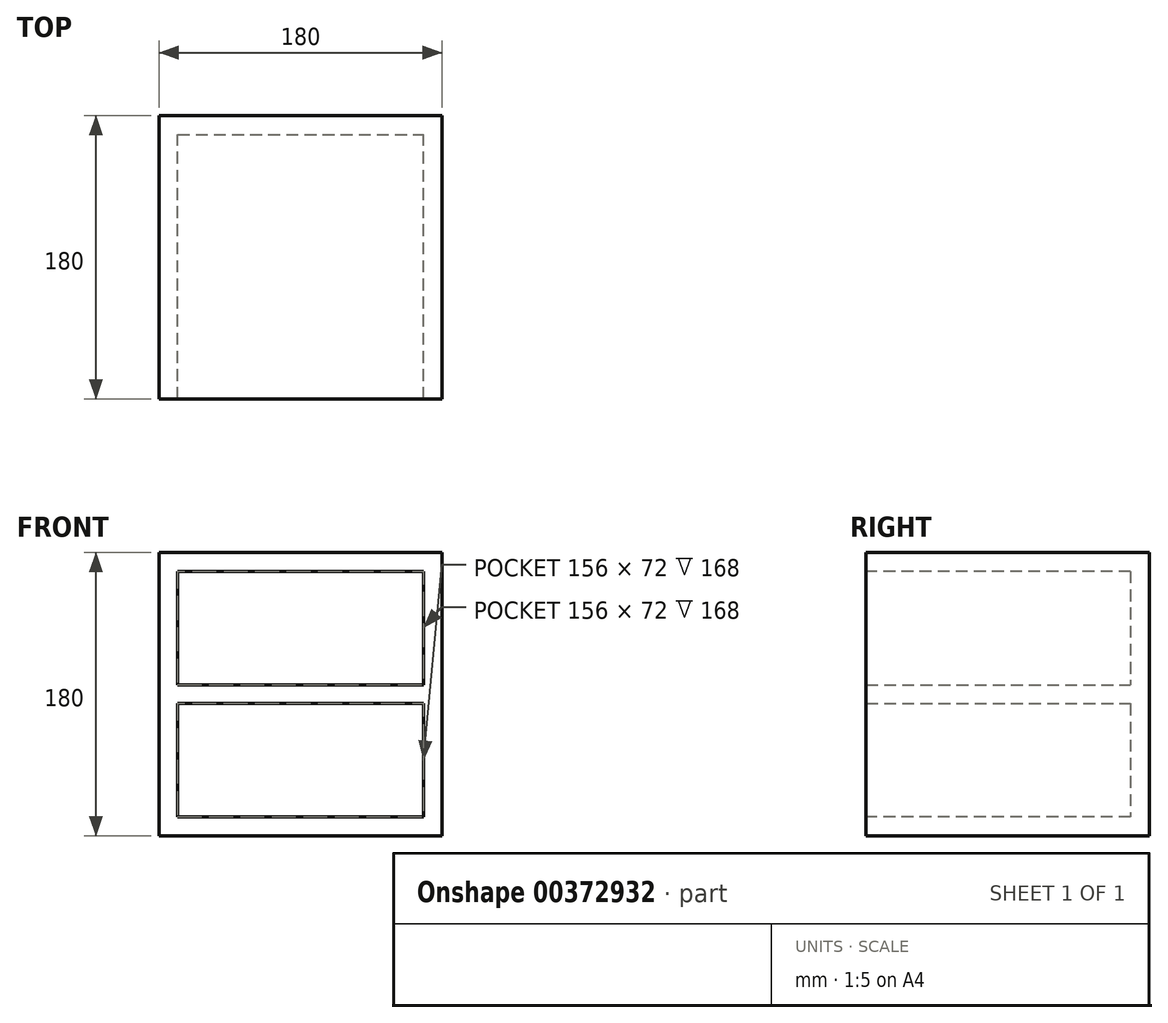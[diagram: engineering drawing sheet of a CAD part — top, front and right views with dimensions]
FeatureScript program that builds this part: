
annotation { "Feature Type Name" : "Feature", "Feature Type Description" : "" }
export const myFeature = defineFeature(function(context is Context, id is Id, definition is map)
    precondition{}
    {
        {
            var Q0;
            Q0=qCreatedBy(makeId("Top.planeOp"),FACE);
            var sketch = newSketch(context, id + "F0", { "sketchPlane" : qUnion([Q0])});
            skLineSegment(sketch, "E0.bottom", {"start": v(-90, 90) * mm, "end": v(90, 90) * mm});
            skLineSegment(sketch, "E0.top", {"start": v(-90, -90) * mm, "end": v(90, -90) * mm});
            skLineSegment(sketch, "E0.left", {"start": v(-90, 90) * mm, "end": v(-90, -90) * mm});
            skLineSegment(sketch, "E0.right", {"start": v(90, 90) * mm, "end": v(90, -90) * mm});
            skPoint(sketch, "E0.middle", {"position": v(0, 0) * mm});
            skSolve(sketch);
        }
        {
            var Q0;
            Q0=makeQuery(id+"F0.imprint","IMPRINT",FACE,{"disambiguationData":[TD([[makeQuery(id+"F0.imprint","IMPRINT",EDGE,{"derivedFrom":sQuery(id+"F0.wireOp",EDGE,"E0.bottom")}),-1.0]])]});
            extrude(context, id + "F1", {"entities" : qUnion([Q0]), "endBound" : BoundingType.SYMMETRIC, "depth" : 180 * mm});
        }
        {
            var Q0;
            Q0=makeQuery(id+"F1.opExtrude","SWEPT_FACE",FACE,{"disambiguationData":[OSD([sQuery(id+"F0.wireOp",EDGE,"E0.top")])]});
            shell(context, id + "F2", {"entities" : qUnion([Q0]), "thickness" : 12 * mm});
        }
        {
            var Q0;
            Q0=makeQuery(id+"F2.opShell","OFFSET_FACE",FACE,{"disambiguationData":[OSD([sQuery(id+"F0.wireOp",EDGE,"E0.bottom")])]});
            var sketch = newSketch(context, id + "F3", { "sketchPlane" : qUnion([Q0])});
            skLineSegment(sketch, "E1.bottom", {"start": v(-84.06, 6) * mm, "end": v(84.06, 6) * mm});
            skLineSegment(sketch, "E1.top", {"start": v(-84.06, -6) * mm, "end": v(84.06, -6) * mm});
            skLineSegment(sketch, "E1.left", {"start": v(-84.06, 6) * mm, "end": v(-84.06, -6) * mm});
            skLineSegment(sketch, "E1.right", {"start": v(84.06, 6) * mm, "end": v(84.06, -6) * mm});
            skPoint(sketch, "E1.middle", {"position": v(0, 0) * mm});
            skSolve(sketch);
        }
        {
            var Q0;
            {var subQ0=sQuery(id+"F3.wireOp",EDGE,"E1.bottom");var subQ1=sQuery(id+"F0.wireOp",EDGE,"E0.bottom");var subQ2=makeQuery(id+"F2.opShell","OFFSET_EDGE",EDGE,{"disambiguationData":[OSD([subQ1,sQuery(id+"F0.wireOp",EDGE,"E0.left")])]});var subQ3=makeQuery(id+"F3.imprint","INTERSECT",VERTEX,{"derivedFrom":[subQ2,subQ0]});Q0=makeQuery(id+"F3.imprint","IMPRINT",FACE,{"disambiguationData":[TD([[makeQuery(id+"F3.imprint","IMPRINT",EDGE,{"disambiguationData":[TD([[subQ3,-1.0]])],"derivedFrom":subQ0}),-1.0]])]});}
            extrude(context, id + "F4", {"entities" : qUnion([Q0]), "operationType" : NewBodyOperationType.ADD, "depth" : 168 * mm});
        }
    });
